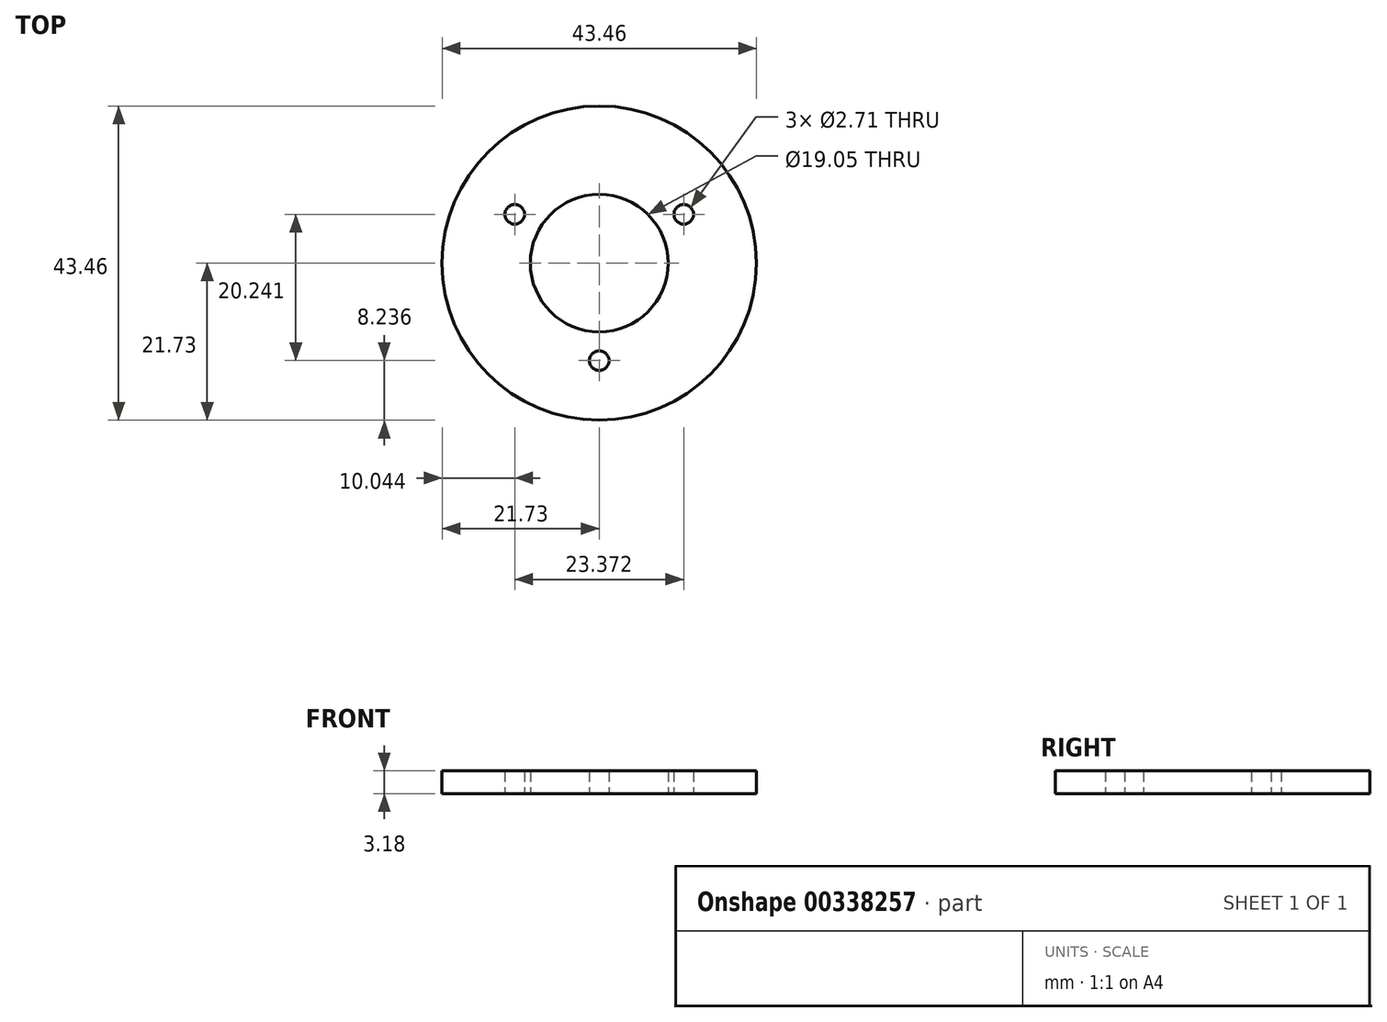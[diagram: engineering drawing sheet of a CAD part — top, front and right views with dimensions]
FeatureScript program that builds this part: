
annotation { "Feature Type Name" : "Feature", "Feature Type Description" : "" }
export const myFeature = defineFeature(function(context is Context, id is Id, definition is map)
    precondition{}
    {
        {
            var Q0;
            Q0=qCreatedBy(makeId("Top.planeOp"),FACE);
            var sketch = newSketch(context, id + "F0", { "sketchPlane" : qUnion([Q0])});
            skCircle(sketch, "E0", {"center": v(0, 0) * mm, "radius": 9.52 * mm});
            skCircle(sketch, "E1", {"center": v(0, 0) * mm, "radius": 21.73 * mm});
            skLineSegment(sketch, "E2", {"start": v(0, 0) * mm, "end": v(0, -13.5) * mm, "construction": true});
            skLineSegment(sketch, "E3", {"start": v(0, -13.5) * mm, "end": v(11.69, 6.75) * mm, "construction": true});
            skLineSegment(sketch, "E4", {"start": v(11.69, 6.75) * mm, "end": v(0, 0) * mm, "construction": true});
            skLineSegment(sketch, "E5", {"start": v(0, 0) * mm, "end": v(-11.69, 6.75) * mm, "construction": true});
            skLineSegment(sketch, "E6", {"start": v(-11.69, 6.75) * mm, "end": v(0, -13.5) * mm, "construction": true});
            skLineSegment(sketch, "E7", {"start": v(-11.69, 6.75) * mm, "end": v(11.69, 6.75) * mm, "construction": true});
            skCircle(sketch, "E8", {"center": v(0, -13.5) * mm, "radius": 3.97 * mm, "construction": true});
            skCircle(sketch, "E9", {"center": v(-11.69, 6.75) * mm, "radius": 1.35 * mm});
            skCircle(sketch, "E10", {"center": v(11.69, 6.75) * mm, "radius": 1.35 * mm});
            skCircle(sketch, "E11", {"center": v(0, -13.5) * mm, "radius": 1.35 * mm});
            skSolve(sketch);
        }
        {
            var Q0;
            Q0=qSketchRegion(id+"F0",true);
            extrude(context, id + "F1", {"entities" : qUnion([Q0]), "depth" : 3.17 * mm});
        }
    });
